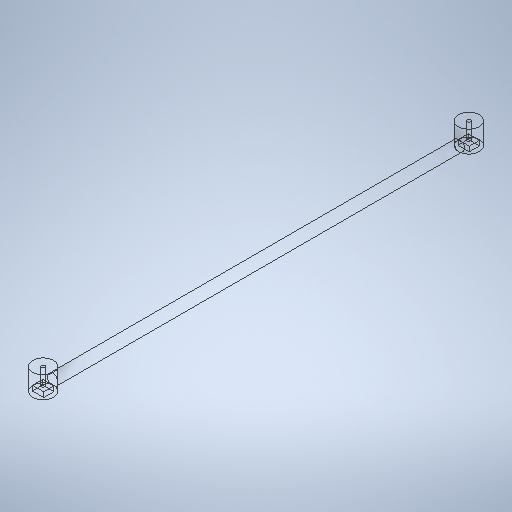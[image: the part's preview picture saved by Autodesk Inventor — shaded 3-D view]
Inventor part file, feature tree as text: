
AUTODESK INVENTOR PART (.ipt)
format: ipt  version: 2025 (Build 290162010, 162A)  size: 298,496 bytes
history: native  units: in
note: dims shown in document units (in); Inventor stores cm internally (conversion verified against a paired STEP export)
features: sketch x4, extrude x3, hole x1
ambient origin geometry x8: Origin, YZ Plane, XZ Plane, XY Plane, X Axis, Y Axis, Z Axis, Center Point
bodies: Solid1 (feature_tree)
feature tree (8):
  extrude  "Extrusion1"  Depth=0.25in TaperAngle=0.0deg
  extrude  "Extrusion2"  Depth=5.1132in
  hole  "Hole1"  [1 undecoded]
  extrude  "Extrusion6"  Depth=0.2717in
  sketch  "Sketch1"  dims[d0=0.25in d1=10.1969in d2=0.0in]
  sketch  "Sketch2"  dims[d4=10.2264in d5=5.1132in]
  sketch  "Sketch3"  dims[d6=0.5in d7=0.5in]
  sketch  "Sketch9"  dims[d8=0.3937in d9=0.125in d10=0.0in d11=0.0in d12=0.0849in d13=0.224in d14=0.325in d15=0.25in d16=0.5635in d17=1.0in d18=0.0in d28=0.2717in d29=0.2441in d30=0.1181in d31=0.0in]
note: 1 required parameter value undecoded (feature->parameter linkage not recoverable at this tier; creation-order binding heuristic only, values carry confidence <= 0.55)
